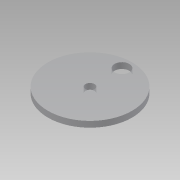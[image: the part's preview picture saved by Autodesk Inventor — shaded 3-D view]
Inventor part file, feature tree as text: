
AUTODESK INVENTOR PART (.ipt)
format: ipt  version: 2015 (Build 190159000, 159)  size: 79,872 bytes
history: native  units: mm
features: extrude x1, sketch x1
ambient origin geometry x8: Origin, YZ Plane, XZ Plane, XY Plane, X Axis, Y Axis, Z Axis, Center Point
bodies: Body1 (feature_tree)
feature tree (2):
  extrude  "Extrusion2"  Depth=6.0mm
  sketch  "Sketch1"  dims[d0=85.5mm d1=9.18mm d4=15.0mm d6=32.5mm d7=6.0mm d8=0.0mm]
